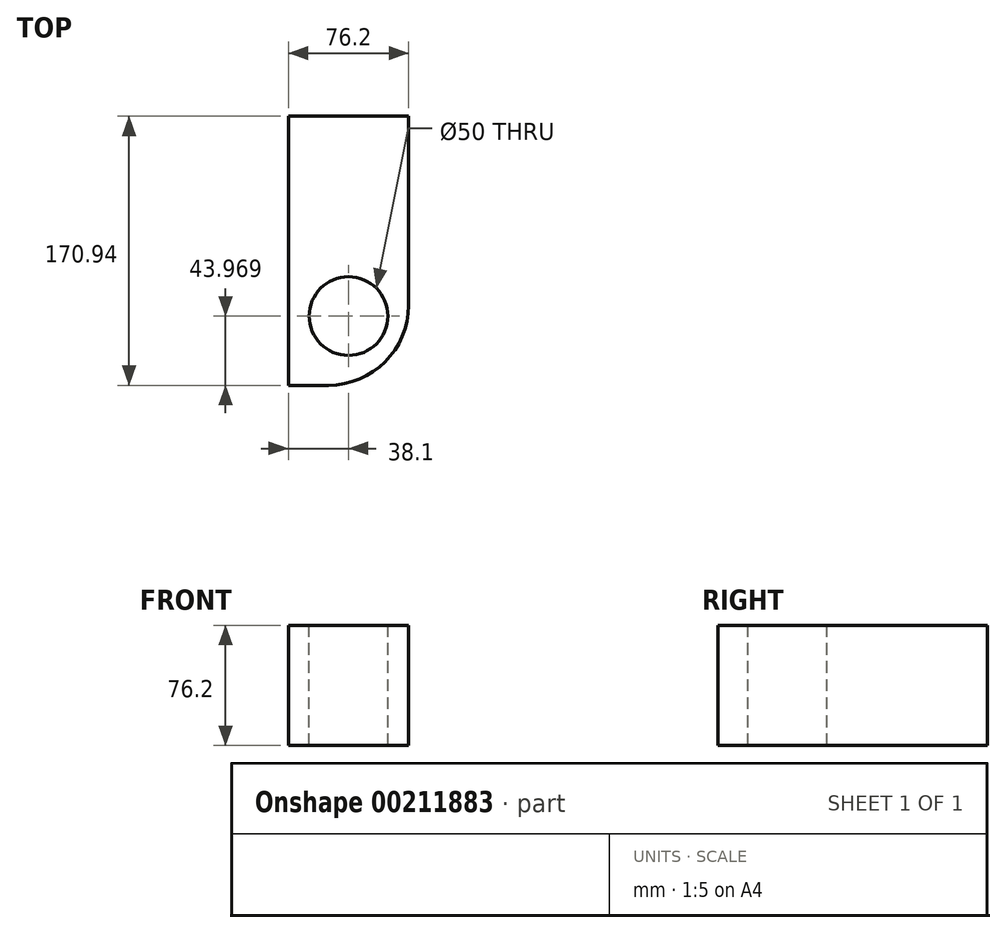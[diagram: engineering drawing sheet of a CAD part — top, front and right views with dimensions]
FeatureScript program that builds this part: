
annotation { "Feature Type Name" : "Feature", "Feature Type Description" : "" }
export const myFeature = defineFeature(function(context is Context, id is Id, definition is map)
    precondition{}
    {
        {
            var Q0;
            Q0=qCreatedBy(makeId("Front.planeOp"),FACE);
            var sketch = newSketch(context, id + "F0", { "sketchPlane" : qUnion([Q0])});
            skLineSegment(sketch, "E0.bottom", {"start": v(-38.1, 38.1) * mm, "end": v(38.1, 38.1) * mm});
            skLineSegment(sketch, "E0.top", {"start": v(-38.1, -38.1) * mm, "end": v(38.1, -38.1) * mm});
            skLineSegment(sketch, "E0.left", {"start": v(-38.1, 38.1) * mm, "end": v(-38.1, -38.1) * mm});
            skLineSegment(sketch, "E0.right", {"start": v(38.1, 38.1) * mm, "end": v(38.1, -38.1) * mm});
            skSolve(sketch);
        }
        {
            var Q0;
            Q0 = qSketchRegion(id + "F0", true);
            extrude(context, id + "F1", {"entities" : qUnion([Q0]), "depth" : 170.94 * mm});
        }
        {
            var Q0;
            Q0=makeQuery(id+"F1.opExtrude","SWEPT_FACE",FACE,{"disambiguationData":[OSD([sQuery(id+"F0.wireOp",EDGE,"E0.bottom")])]});
            var sketch = newSketch(context, id + "F2", { "sketchPlane" : qUnion([Q0])});
            skCircle(sketch, "E1", {"center": v(0, -126.97) * mm, "radius": 25 * mm});
            skSolve(sketch);
        }
        {
            var Q0;
            Q0 = qSketchRegion(id + "F2", true);
            extrude(context, id + "F3", {"entities" : qUnion([Q0]), "operationType" : NewBodyOperationType.REMOVE, "endBound" : BoundingType.THROUGH_ALL, "oppositeDirection" : true, "depth" : 47.75 * mm});
        }
        {
            var Q0;
            Q0=makeQuery(id+"F1.opExtrude","CAP_EDGE",EDGE,{"disambiguationData":[OSD([sQuery(id+"F0.wireOp",EDGE,"E0.right")])],"isStart":false});
            fillet(context, id + "F4", {"entities" : qUnion([Q0]), "radius" : 50.8 * mm, "tangentPropagation" : true, "allowEdgeOverflow" : false});
        }
    });
